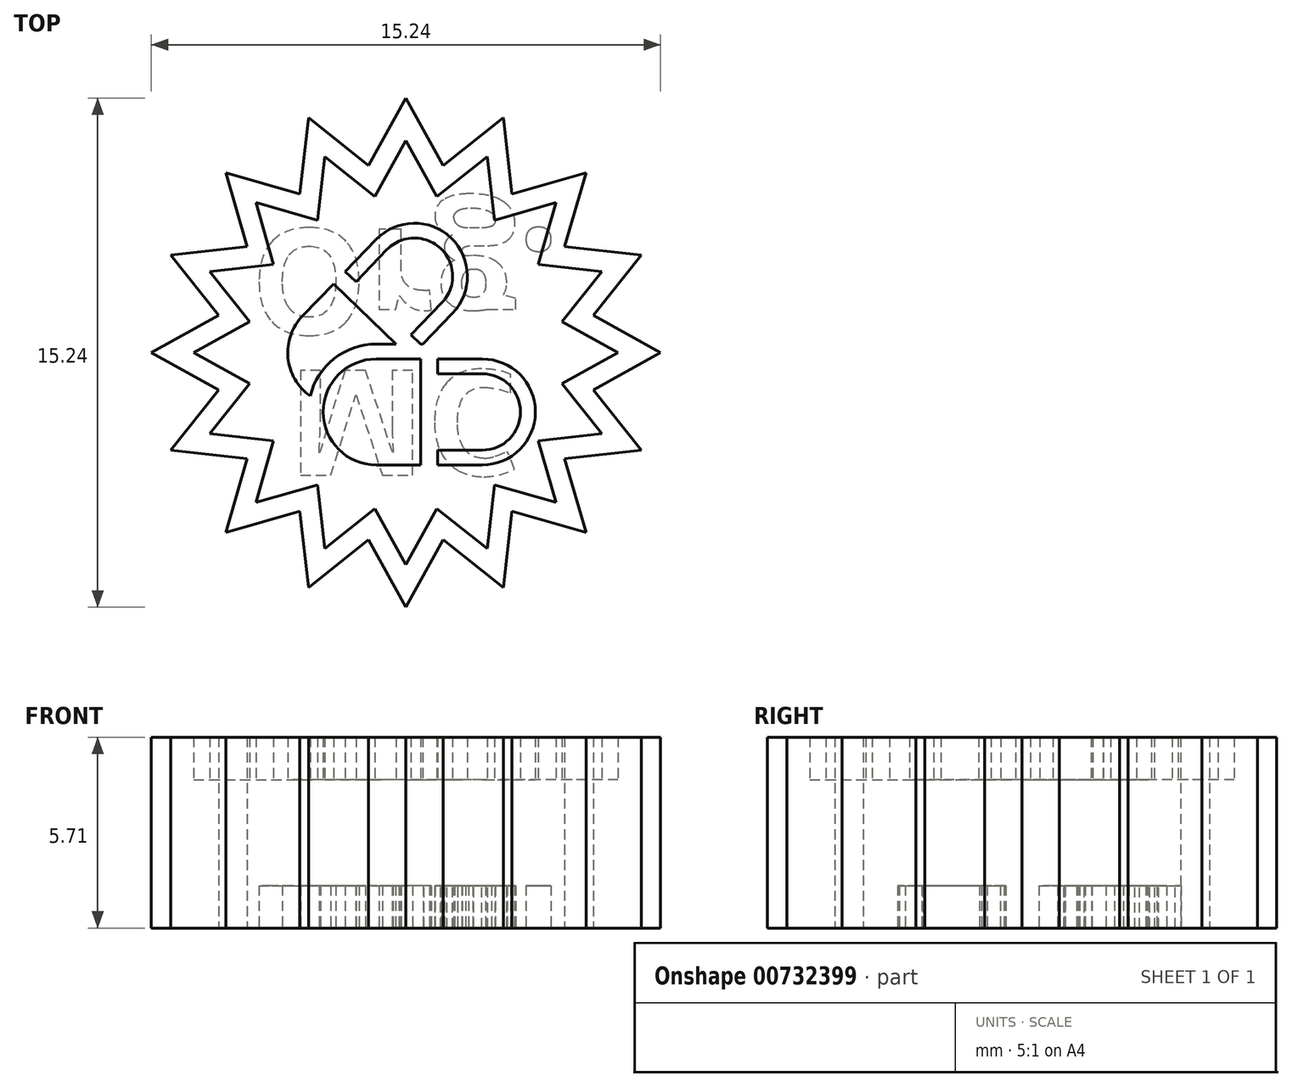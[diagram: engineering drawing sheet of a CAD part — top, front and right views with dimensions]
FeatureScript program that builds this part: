
annotation { "Feature Type Name" : "Feature", "Feature Type Description" : "" }
export const myFeature = defineFeature(function(context is Context, id is Id, definition is map)
    precondition{}
    {
        {
            var Q0;
            Q0=qCreatedBy(makeId("Top.planeOp"),FACE);
            var sketch = newSketch(context, id + "F0", { "sketchPlane" : qUnion([Q0])});
            skCircle(sketch, "E0", {"center": v(0, 0) * mm, "radius": 7.62 * mm, "construction": true});
            skLineSegment(sketch, "E1", {"start": v(0, 0) * mm, "end": v(0, 11.04) * mm, "construction": true});
            skLineSegment(sketch, "E2", {"start": v(2.92, 7.04) * mm, "end": v(0, 0) * mm, "construction": true});
            skLineSegment(sketch, "E3", {"start": v(0, 0) * mm, "end": v(1.49, 7.47) * mm, "construction": true});
            skCircle(sketch, "E4", {"center": v(0, 0) * mm, "radius": 5.72 * mm, "construction": true});
            skLineSegment(sketch, "E5.MirrorCS", {"start": v(0, 0) * mm, "end": v(4.23, 6.34) * mm, "construction": true});
            skLineSegment(sketch, "E6.MirrorCS", {"start": v(0, 0) * mm, "end": v(7.8, 7.8) * mm, "construction": true});
            skLineSegment(sketch, "E7.MirrorCS", {"start": v(0, 0) * mm, "end": v(6.34, 4.23) * mm, "construction": true});
            skLineSegment(sketch, "E8.MirrorCS", {"start": v(7.04, 2.92) * mm, "end": v(0, 0) * mm, "construction": true});
            skLineSegment(sketch, "E9.MirrorCS", {"start": v(0, 0) * mm, "end": v(7.47, 1.49) * mm, "construction": true});
            skLineSegment(sketch, "E10.MirrorCS", {"start": v(0, 0) * mm, "end": v(11.04, 0) * mm, "construction": true});
            skLineSegment(sketch, "E11", {"start": v(0, 7.62) * mm, "end": v(1.11, 5.6) * mm});
            skLineSegment(sketch, "E12", {"start": v(1.11, 5.6) * mm, "end": v(2.92, 7.04) * mm});
            skLineSegment(sketch, "E13", {"start": v(2.92, 7.04) * mm, "end": v(3.18, 4.75) * mm});
            skLineSegment(sketch, "E14", {"start": v(3.18, 4.75) * mm, "end": v(5.39, 5.39) * mm});
            skLineSegment(sketch, "E15", {"start": v(5.39, 5.39) * mm, "end": v(4.75, 3.18) * mm});
            skLineSegment(sketch, "E16", {"start": v(4.75, 3.18) * mm, "end": v(7.04, 2.92) * mm});
            skLineSegment(sketch, "E17", {"start": v(7.04, 2.92) * mm, "end": v(5.6, 1.11) * mm});
            skLineSegment(sketch, "E18", {"start": v(5.6, 1.11) * mm, "end": v(7.62, 0) * mm});
            skLineSegment(sketch, "E19", {"start": v(7.62, 0) * mm, "end": v(7.62, 0) * mm});
            skLineSegment(sketch, "E20.MirrorCS", {"start": v(5.6, -1.11) * mm, "end": v(7.62, 0) * mm});
            skLineSegment(sketch, "E21.MirrorCS", {"start": v(7.04, -2.92) * mm, "end": v(5.6, -1.11) * mm});
            skLineSegment(sketch, "E22.MirrorCS", {"start": v(4.75, -3.18) * mm, "end": v(7.04, -2.92) * mm});
            skLineSegment(sketch, "E23.MirrorCS", {"start": v(5.39, -5.39) * mm, "end": v(4.75, -3.18) * mm});
            skLineSegment(sketch, "E24.MirrorCS", {"start": v(3.18, -4.75) * mm, "end": v(5.39, -5.39) * mm});
            skLineSegment(sketch, "E25.MirrorCS", {"start": v(2.92, -7.04) * mm, "end": v(3.18, -4.75) * mm});
            skLineSegment(sketch, "E26.MirrorCS", {"start": v(1.11, -5.6) * mm, "end": v(2.92, -7.04) * mm});
            skLineSegment(sketch, "E27.MirrorCS", {"start": v(0, -7.62) * mm, "end": v(1.11, -5.6) * mm});
            skLineSegment(sketch, "E28.MirrorCS", {"start": v(0, 7.62) * mm, "end": v(-1.11, 5.6) * mm});
            skLineSegment(sketch, "E29.MirrorCS", {"start": v(-1.11, 5.6) * mm, "end": v(-2.92, 7.04) * mm});
            skLineSegment(sketch, "E30.MirrorCS", {"start": v(-2.92, 7.04) * mm, "end": v(-3.18, 4.75) * mm});
            skLineSegment(sketch, "E31.MirrorCS", {"start": v(-3.18, 4.75) * mm, "end": v(-5.39, 5.39) * mm});
            skLineSegment(sketch, "E32.MirrorCS", {"start": v(-5.39, 5.39) * mm, "end": v(-4.75, 3.18) * mm});
            skLineSegment(sketch, "E33.MirrorCS", {"start": v(-4.75, 3.18) * mm, "end": v(-7.04, 2.92) * mm});
            skLineSegment(sketch, "E34.MirrorCS", {"start": v(-7.04, 2.92) * mm, "end": v(-5.6, 1.11) * mm});
            skLineSegment(sketch, "E35.MirrorCS", {"start": v(-5.6, 1.11) * mm, "end": v(-7.62, 0) * mm});
            skLineSegment(sketch, "E36.MirrorCS", {"start": v(-5.6, -1.11) * mm, "end": v(-7.62, 0) * mm});
            skLineSegment(sketch, "E37.MirrorCS", {"start": v(-7.04, -2.92) * mm, "end": v(-5.6, -1.11) * mm});
            skLineSegment(sketch, "E38.MirrorCS", {"start": v(-4.75, -3.18) * mm, "end": v(-7.04, -2.92) * mm});
            skLineSegment(sketch, "E39.MirrorCS", {"start": v(-5.39, -5.39) * mm, "end": v(-4.75, -3.18) * mm});
            skLineSegment(sketch, "E40.MirrorCS", {"start": v(-3.18, -4.75) * mm, "end": v(-5.39, -5.39) * mm});
            skLineSegment(sketch, "E41.MirrorCS", {"start": v(-2.92, -7.04) * mm, "end": v(-3.18, -4.75) * mm});
            skLineSegment(sketch, "E42.MirrorCS", {"start": v(-1.11, -5.6) * mm, "end": v(-2.92, -7.04) * mm});
            skLineSegment(sketch, "E43.MirrorCS", {"start": v(0, -7.62) * mm, "end": v(-1.11, -5.6) * mm});
            skCircle(sketch, "E44", {"center": v(0, 0) * mm, "radius": 6.35 * mm, "construction": true});
            skLineSegment(sketch, "E45", {"start": v(0, 6.35) * mm, "end": v(0.93, 4.67) * mm});
            skLineSegment(sketch, "E46.MirrorCS", {"start": v(2.43, 5.87) * mm, "end": v(0.93, 4.67) * mm});
            skLineSegment(sketch, "E47.MirrorCS", {"start": v(2.43, 5.87) * mm, "end": v(2.65, 3.96) * mm});
            skLineSegment(sketch, "E48.MirrorCS", {"start": v(4.5, 4.5) * mm, "end": v(2.65, 3.96) * mm});
            skLineSegment(sketch, "E49.MirrorCS", {"start": v(4.5, 4.5) * mm, "end": v(3.96, 2.65) * mm});
            skLineSegment(sketch, "E50.MirrorCS", {"start": v(5.87, 2.43) * mm, "end": v(3.96, 2.65) * mm});
            skLineSegment(sketch, "E51.MirrorCS", {"start": v(5.87, 2.43) * mm, "end": v(4.67, 0.93) * mm});
            skLineSegment(sketch, "E52.MirrorCS", {"start": v(6.35, 0) * mm, "end": v(4.67, 0.93) * mm});
            skLineSegment(sketch, "E53.MirrorCS", {"start": v(6.35, 0) * mm, "end": v(4.67, -0.93) * mm});
            skLineSegment(sketch, "E54.MirrorCS", {"start": v(5.87, -2.43) * mm, "end": v(4.67, -0.93) * mm});
            skLineSegment(sketch, "E55.MirrorCS", {"start": v(5.87, -2.43) * mm, "end": v(3.96, -2.65) * mm});
            skLineSegment(sketch, "E56.MirrorCS", {"start": v(4.5, -4.5) * mm, "end": v(3.96, -2.65) * mm});
            skLineSegment(sketch, "E57.MirrorCS", {"start": v(4.5, -4.5) * mm, "end": v(2.65, -3.96) * mm});
            skLineSegment(sketch, "E58.MirrorCS", {"start": v(2.43, -5.87) * mm, "end": v(2.65, -3.96) * mm});
            skLineSegment(sketch, "E59.MirrorCS", {"start": v(2.43, -5.87) * mm, "end": v(0.93, -4.67) * mm});
            skLineSegment(sketch, "E60.MirrorCS", {"start": v(0, -6.35) * mm, "end": v(0.93, -4.67) * mm});
            skLineSegment(sketch, "E61.MirrorCS", {"start": v(0, 6.35) * mm, "end": v(-0.93, 4.67) * mm});
            skLineSegment(sketch, "E62.MirrorCS", {"start": v(-2.43, 5.87) * mm, "end": v(-0.93, 4.67) * mm});
            skLineSegment(sketch, "E63.MirrorCS", {"start": v(-2.43, 5.87) * mm, "end": v(-2.65, 3.96) * mm});
            skLineSegment(sketch, "E64.MirrorCS", {"start": v(-4.5, 4.5) * mm, "end": v(-2.65, 3.96) * mm});
            skLineSegment(sketch, "E65.MirrorCS", {"start": v(-4.5, 4.5) * mm, "end": v(-3.96, 2.65) * mm});
            skLineSegment(sketch, "E66.MirrorCS", {"start": v(-5.87, 2.43) * mm, "end": v(-3.96, 2.65) * mm});
            skLineSegment(sketch, "E67.MirrorCS", {"start": v(-5.87, 2.43) * mm, "end": v(-4.67, 0.93) * mm});
            skLineSegment(sketch, "E68.MirrorCS", {"start": v(-6.35, 0) * mm, "end": v(-4.67, 0.93) * mm});
            skLineSegment(sketch, "E69.MirrorCS", {"start": v(-6.35, 0) * mm, "end": v(-4.67, -0.93) * mm});
            skLineSegment(sketch, "E70.MirrorCS", {"start": v(-5.87, -2.43) * mm, "end": v(-4.67, -0.93) * mm});
            skLineSegment(sketch, "E71.MirrorCS", {"start": v(-5.87, -2.43) * mm, "end": v(-3.96, -2.65) * mm});
            skLineSegment(sketch, "E72.MirrorCS", {"start": v(-4.5, -4.5) * mm, "end": v(-3.96, -2.65) * mm});
            skLineSegment(sketch, "E73.MirrorCS", {"start": v(-4.5, -4.5) * mm, "end": v(-2.65, -3.96) * mm});
            skLineSegment(sketch, "E74.MirrorCS", {"start": v(-2.43, -5.87) * mm, "end": v(-2.65, -3.96) * mm});
            skLineSegment(sketch, "E75.MirrorCS", {"start": v(-2.43, -5.87) * mm, "end": v(-0.93, -4.67) * mm});
            skLineSegment(sketch, "E76.MirrorCS", {"start": v(0, -6.35) * mm, "end": v(-0.93, -4.67) * mm});
            skSolve(sketch);
        }
        {
            var Q0;
            Q0=makeQuery(id+"F0.imprint","IMPRINT",FACE,{"disambiguationData":[TD([[makeQuery(id+"F0.imprint","IMPRINT",EDGE,{"derivedFrom":sQuery(id+"F0.wireOp",EDGE,"E11")}),-1.0]])]});
            extrude(context, id + "F1", {"entities" : qUnion([Q0]), "depth" : 5.7 * mm, "offsetDistance" : 25.4 * mm});
        }
        {
            var Q0;
            Q0=makeQuery(id+"F0.imprint","IMPRINT",FACE,{"disambiguationData":[TD([[makeQuery(id+"F0.imprint","IMPRINT",EDGE,{"derivedFrom":sQuery(id+"F0.wireOp",EDGE,"E46.MirrorCS")}),1.0]])]});
            extrude(context, id + "F2", {"entities" : qUnion([Q0]), "operationType" : NewBodyOperationType.ADD, "depth" : 4.44 * mm, "offsetDistance" : 25.4 * mm});
        }
        {
            var Q0;
            Q0=qCreatedBy(makeId("Top.planeOp"),FACE);
            var sketch = newSketch(context, id + "F3", { "sketchPlane" : qUnion([Q0])});
            skArc(sketch, "E77", {"start": v(2.29, -3.37) * mm, "mid": v(3.87, -1.78) * mm, "end": v(2.29, -0.2) * mm});
            skLineSegment(sketch, "E78", {"start": v(0, 6.21) * mm, "end": v(0, -6.92) * mm, "construction": true});
            skLineSegment(sketch, "E79", {"start": v(2.29, -1.78) * mm, "end": v(-7.57, -1.78) * mm, "construction": true});
            skArc(sketch, "E80", {"start": v(-0.89, -0.2) * mm, "mid": v(-2.48, -1.78) * mm, "end": v(-0.89, -3.37) * mm});
            skLineSegment(sketch, "E81", {"start": v(-0.89, -0.2) * mm, "end": v(0.44, -0.2) * mm});
            skLineSegment(sketch, "E82.MirrorCS", {"start": v(-0.89, -3.37) * mm, "end": v(0.44, -3.37) * mm});
            skLineSegment(sketch, "E83", {"start": v(0.7, -0.2) * mm, "end": v(0.7, -3.37) * mm, "construction": true});
            skLineSegment(sketch, "E84", {"start": v(0.44, -0.2) * mm, "end": v(0.44, -3.37) * mm});
            skLineSegment(sketch, "E85.MirrorCS", {"start": v(0.95, -0.2) * mm, "end": v(0.95, -0.63) * mm});
            skArc(sketch, "E86", {"start": v(2.29, -2.92) * mm, "mid": v(3.43, -1.78) * mm, "end": v(2.29, -0.63) * mm});
            skLineSegment(sketch, "E87", {"start": v(2.29, -0.63) * mm, "end": v(0.95, -0.63) * mm});
            skLineSegment(sketch, "E88.trimOffspring", {"start": v(0.95, -0.2) * mm, "end": v(2.29, -0.2) * mm});
            skLineSegment(sketch, "E89.MirrorCS", {"start": v(2.29, -2.92) * mm, "end": v(0.95, -2.92) * mm});
            skLineSegment(sketch, "E90.trimOffspring", {"start": v(0.95, -2.92) * mm, "end": v(0.95, -3.37) * mm});
            skLineSegment(sketch, "E91.trimOffspring", {"start": v(0.95, -3.37) * mm, "end": v(2.29, -3.37) * mm});
            skSolve(sketch);
        }
        {
            var Q0;
            Q0=makeQuery(id+"F3.imprint","IMPRINT",FACE,{"disambiguationData":[TD([[makeQuery(id+"F3.imprint","IMPRINT",EDGE,{"derivedFrom":sQuery(id+"F3.wireOp",EDGE,"E80")}),1.0]])]});
            var Q1;
            Q1=makeQuery(id+"F3.imprint","IMPRINT",FACE,{"disambiguationData":[TD([[makeQuery(id+"F3.imprint","IMPRINT",EDGE,{"derivedFrom":sQuery(id+"F3.wireOp",EDGE,"E77")}),1.0]])]});
            extrude(context, id + "F4", {"entities" : qUnion([Q0, Q1]), "operationType" : NewBodyOperationType.ADD, "depth" : 5.7 * mm, "offsetDistance" : 25.4 * mm});
        }
        {
            var Q0;
            Q0=qCreatedBy(makeId("Top.planeOp"),FACE);
            var sketch = newSketch(context, id + "F5", { "sketchPlane" : qUnion([Q0])});
            skArc(sketch, "E92", {"start": v(-3.1, 1.1) * mm, "mid": v(-3.53, -0.15) * mm, "end": v(-2.86, -1.3) * mm});
            skLineSegment(sketch, "E93", {"start": v(-1.95, 0) * mm, "end": v(0.25, 2.29) * mm, "construction": true});
            skLineSegment(sketch, "E94", {"start": v(-3.1, 1.1) * mm, "end": v(-2.17, 2.06) * mm});
            skArc(sketch, "E95", {"start": v(1.08, 1.5) * mm, "mid": v(1.05, 3.1) * mm, "end": v(-0.57, 3.08) * mm});
            skLineSegment(sketch, "E96", {"start": v(-2, 2.24) * mm, "end": v(0.3, 0.04) * mm, "construction": true});
            skLineSegment(sketch, "E97", {"start": v(-2.17, 2.06) * mm, "end": v(-0.3, 0.25) * mm});
            skLineSegment(sketch, "E98.MirrorCS", {"start": v(-1.81, 2.43) * mm, "end": v(-1.5, 2.12) * mm});
            skLineSegment(sketch, "E99", {"start": v(-0.57, 3.08) * mm, "end": v(-1.5, 2.12) * mm});
            skLineSegment(sketch, "E100.MirrorCS", {"start": v(1.08, 1.5) * mm, "end": v(0.15, 0.53) * mm});
            skPoint(sketch, "E101.orphan", {"position": v(0.12, 3.8) * mm});
            skPoint(sketch, "E102.orphan", {"position": v(1.77, 2.2) * mm});
            skArc(sketch, "E103.trimOffspring", {"start": v(1.4, 1.18) * mm, "mid": v(1.36, 3.43) * mm, "end": v(-0.89, 3.39) * mm});
            skLineSegment(sketch, "E104", {"start": v(-0.89, 0.25) * mm, "end": v(-0.3, 0.25) * mm});
            skArc(sketch, "E105.trimOffspring", {"start": v(-0.89, 0.25) * mm, "mid": v(-2.14, -0.18) * mm, "end": v(-2.86, -1.3) * mm});
            skPoint(sketch, "E106.orphan", {"position": v(-1.98, 1.62) * mm});
            skLineSegment(sketch, "E107.trimOffspring", {"start": v(0.44, 0.25) * mm, "end": v(0.5, 0.25) * mm});
            skPoint(sketch, "E108.orphan", {"position": v(0.47, 0.22) * mm});
            skLineSegment(sketch, "E109.trimOffspring", {"start": v(0.5, 0.25) * mm, "end": v(1.4, 1.18) * mm});
            skPoint(sketch, "E110.orphan", {"position": v(-0.8, -1.1) * mm});
            skPoint(sketch, "E111.orphan", {"position": v(0.12, -0.14) * mm});
            skPoint(sketch, "E112.orphan", {"position": v(-0.33, 0.03) * mm});
            skLineSegment(sketch, "E113.trimOffspring", {"start": v(0.15, 0.53) * mm, "end": v(0.44, 0.25) * mm});
            skLineSegment(sketch, "E114.trimOffspring", {"start": v(-1.81, 2.43) * mm, "end": v(-0.89, 3.39) * mm});
            skSolve(sketch);
        }
        {
            var Q0;
            Q0=makeQuery(id+"F5.imprint","IMPRINT",FACE,{"disambiguationData":[TD([[makeQuery(id+"F5.imprint","IMPRINT",EDGE,{"derivedFrom":sQuery(id+"F5.wireOp",EDGE,"E95")}),-1.0]])]});
            var Q1;
            Q1=makeQuery(id+"F5.imprint","IMPRINT",FACE,{"disambiguationData":[TD([[makeQuery(id+"F5.imprint","IMPRINT",EDGE,{"derivedFrom":sQuery(id+"F5.wireOp",EDGE,"E92")}),1.0]])]});
            extrude(context, id + "F6", {"entities" : qUnion([Q0, Q1]), "operationType" : NewBodyOperationType.ADD, "depth" : 5.7 * mm, "offsetDistance" : 25.4 * mm});
        }
        {
            var Q0;
            {var subQ0=sQuery(id+"F0.wireOp",EDGE,"E76.MirrorCS");var subQ1=sQuery(id+"F0.wireOp",EDGE,"E75.MirrorCS");var subQ2=sQuery(id+"F0.wireOp",EDGE,"E74.MirrorCS");var subQ3=sQuery(id+"F0.wireOp",EDGE,"E73.MirrorCS");var subQ4=sQuery(id+"F0.wireOp",EDGE,"E72.MirrorCS");var subQ5=sQuery(id+"F0.wireOp",EDGE,"E71.MirrorCS");var subQ6=sQuery(id+"F0.wireOp",EDGE,"E70.MirrorCS");var subQ7=sQuery(id+"F0.wireOp",EDGE,"E69.MirrorCS");var subQ8=sQuery(id+"F0.wireOp",EDGE,"E68.MirrorCS");var subQ9=sQuery(id+"F0.wireOp",EDGE,"E67.MirrorCS");var subQ10=sQuery(id+"F0.wireOp",EDGE,"E66.MirrorCS");var subQ11=sQuery(id+"F0.wireOp",EDGE,"E65.MirrorCS");var subQ12=sQuery(id+"F0.wireOp",EDGE,"E64.MirrorCS");var subQ13=sQuery(id+"F0.wireOp",EDGE,"E63.MirrorCS");var subQ14=sQuery(id+"F0.wireOp",EDGE,"E45");var subQ15=sQuery(id+"F0.wireOp",EDGE,"E62.MirrorCS");var subQ16=sQuery(id+"F0.wireOp",EDGE,"E61.MirrorCS");var subQ17=sQuery(id+"F0.wireOp",EDGE,"E60.MirrorCS");var subQ18=sQuery(id+"F0.wireOp",EDGE,"E59.MirrorCS");var subQ19=sQuery(id+"F0.wireOp",EDGE,"E58.MirrorCS");var subQ20=sQuery(id+"F0.wireOp",EDGE,"E57.MirrorCS");var subQ21=sQuery(id+"F0.wireOp",EDGE,"E56.MirrorCS");var subQ22=sQuery(id+"F0.wireOp",EDGE,"E55.MirrorCS");var subQ23=sQuery(id+"F0.wireOp",EDGE,"E54.MirrorCS");var subQ24=sQuery(id+"F0.wireOp",EDGE,"E53.MirrorCS");var subQ25=sQuery(id+"F0.wireOp",EDGE,"E52.MirrorCS");var subQ26=sQuery(id+"F0.wireOp",EDGE,"E51.MirrorCS");var subQ27=sQuery(id+"F0.wireOp",EDGE,"E50.MirrorCS");var subQ28=sQuery(id+"F0.wireOp",EDGE,"E49.MirrorCS");var subQ29=sQuery(id+"F0.wireOp",EDGE,"E48.MirrorCS");var subQ30=sQuery(id+"F0.wireOp",EDGE,"E47.MirrorCS");var subQ31=sQuery(id+"F0.wireOp",EDGE,"E46.MirrorCS");Q0=makeQuery(id+"F2.boolean.opBoolean","MERGE",FACE,{"derivedFrom":[makeQuery(id+"F1.opExtrude","CAP_FACE",FACE,{"disambiguationData":[OSD([sQuery(id+"F0.wireOp",EDGE,"E11"),sQuery(id+"F0.wireOp",EDGE,"E12"),sQuery(id+"F0.wireOp",EDGE,"E13"),sQuery(id+"F0.wireOp",EDGE,"E14"),sQuery(id+"F0.wireOp",EDGE,"E15"),sQuery(id+"F0.wireOp",EDGE,"E16"),sQuery(id+"F0.wireOp",EDGE,"E17"),sQuery(id+"F0.wireOp",EDGE,"E18"),sQuery(id+"F0.wireOp",EDGE,"E20.MirrorCS"),sQuery(id+"F0.wireOp",EDGE,"E21.MirrorCS"),sQuery(id+"F0.wireOp",EDGE,"E22.MirrorCS"),sQuery(id+"F0.wireOp",EDGE,"E23.MirrorCS"),sQuery(id+"F0.wireOp",EDGE,"E24.MirrorCS"),sQuery(id+"F0.wireOp",EDGE,"E25.MirrorCS"),sQuery(id+"F0.wireOp",EDGE,"E26.MirrorCS"),sQuery(id+"F0.wireOp",EDGE,"E27.MirrorCS"),sQuery(id+"F0.wireOp",EDGE,"E28.MirrorCS"),sQuery(id+"F0.wireOp",EDGE,"E29.MirrorCS"),sQuery(id+"F0.wireOp",EDGE,"E30.MirrorCS"),sQuery(id+"F0.wireOp",EDGE,"E31.MirrorCS"),sQuery(id+"F0.wireOp",EDGE,"E32.MirrorCS"),sQuery(id+"F0.wireOp",EDGE,"E33.MirrorCS"),sQuery(id+"F0.wireOp",EDGE,"E34.MirrorCS"),sQuery(id+"F0.wireOp",EDGE,"E35.MirrorCS"),sQuery(id+"F0.wireOp",EDGE,"E36.MirrorCS"),sQuery(id+"F0.wireOp",EDGE,"E37.MirrorCS"),sQuery(id+"F0.wireOp",EDGE,"E38.MirrorCS"),sQuery(id+"F0.wireOp",EDGE,"E39.MirrorCS"),sQuery(id+"F0.wireOp",EDGE,"E40.MirrorCS"),sQuery(id+"F0.wireOp",EDGE,"E41.MirrorCS"),sQuery(id+"F0.wireOp",EDGE,"E42.MirrorCS"),sQuery(id+"F0.wireOp",EDGE,"E43.MirrorCS"),subQ31,subQ30,subQ29,subQ28,subQ27,subQ26,subQ25,subQ24,subQ23,subQ22,subQ21,subQ20,subQ19,subQ18,subQ17,subQ16,subQ15,subQ14,subQ13,subQ12,subQ11,subQ10,subQ9,subQ8,subQ7,subQ6,subQ5,subQ4,subQ3,subQ2,subQ1,subQ0])],"isStart":true}),makeQuery(id+"F2.opExtrude","CAP_FACE",FACE,{"disambiguationData":[OSD([subQ31,subQ30,subQ29,subQ28,subQ27,subQ26,subQ25,subQ24,subQ23,subQ22,subQ21,subQ20,subQ19,subQ18,subQ17,subQ16,subQ15,subQ14,subQ13,subQ12,subQ11,subQ10,subQ9,subQ8,subQ7,subQ6,subQ5,subQ4,subQ3,subQ2,subQ1,subQ0])],"isStart":true})]});}
            var sketch = newSketch(context, id + "F7", { "sketchPlane" : qUnion([Q0])});
            skText(sketch, "E115", { "text": "MC", "fontName": "OpenSans-Bold.ttf"});
            skText(sketch, "E116", { "text": "Org.", "fontName": "OpenSans-Bold.ttf"});
            skLineSegment(sketch, "E117", {"start": v(0, 7.62) * mm, "end": v(0, -7.62) * mm, "construction": true});
            const initialGuessF7  = {"E115": [-0.00355, 0.00053, 1, 0, 0.00317], "E116": [-0.00465, -0.0037, 1, 0, 0.00317]};
            skSetInitialGuess(sketch, initialGuessF7);
            skSolve(sketch);
        }
        {
            var Q0;
            Q0 = qSketchRegion(id + "F7", true);
            extrude(context, id + "F8", {"entities" : qUnion([Q0]), "operationType" : NewBodyOperationType.REMOVE, "oppositeDirection" : true, "depth" : 1.27 * mm, "offsetDistance" : 25.4 * mm});
        }
    });
